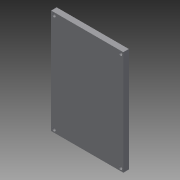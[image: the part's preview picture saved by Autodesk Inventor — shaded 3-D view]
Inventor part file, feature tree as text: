
AUTODESK INVENTOR PART (.ipt)
format: ipt  version: 2015 (Build 190159000, 159)  size: 164,864 bytes
history: native  units: in
note: dims shown in document units (in); Inventor stores cm internally (conversion verified against a paired STEP export)
features: reference x29, extrude x3, sketch x3
ambient origin geometry x8: Origin, YZ Plane, XZ Plane, XY Plane, X Axis, Y Axis, Z Axis, Center Point
bodies: Solid1 (feature_tree)
feature tree (35):
  extrude  "Extrusion1"  Depth=0.4356in
  extrude  "Extrusion2"  Depth=0.5723in
  extrude  "Extrusion3"  Depth=0.6876in
  sketch  "Sketch1"  dims[d0=0.1969in d1=0.0in d2=0.4356in]
  reference  "Reference1"
  reference  "Reference2"
  reference  "Reference3"
  reference  "Reference4"
  reference  "Reference5"
  reference  "Reference6"
  reference  "Reference7"
  reference  "Reference8"
  reference  "Reference9"
  reference  "Reference10"
  reference  "Reference11"
  reference  "Reference12"
  sketch  "Sketch2"  dims[d3=0.6876in d4=0.5723in]
  sketch  "Sketch3"  dims[d5=0.4356in d6=0.6876in d7=0.5723in d8=1.2795in d9=1.2795in d10=0.1181in d11=0.0in d12=0.0787in d13=0.0787in d14=0.0787in d15=0.0787in d16=0.1181in d17=0.0in]
  reference  "Reference17"
  reference  "Reference18"
  reference  "Reference19"
  reference  "Reference20"
  reference  "Reference21"
  reference  "Reference22"
  reference  "Reference23"
  reference  "Reference24"
  reference  "Reference25"
  reference  "Reference26"
  reference  "Reference27"
  reference  "Reference28"
  reference  "Reference29"
  reference  "Reference30"
  reference  "Reference31"
  reference  "Reference32"
  reference  "Reference33"
